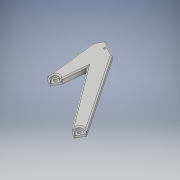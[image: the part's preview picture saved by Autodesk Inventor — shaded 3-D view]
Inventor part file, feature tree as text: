
AUTODESK INVENTOR PART (.ipt)
format: ipt  version: 2019.4 (Build 234330000, 330)  size: 259,584 bytes
history: native  units: mm
features: extrude x4, fillet x4, sketch x4
ambient origin geometry x8: Origin, YZ Plane, XZ Plane, XY Plane, X Axis, Y Axis, Z Axis, Center Point
bodies: Solid1 (feature_tree)
feature tree (12):
  extrude  "Extrusion1"  TaperAngle=90.0deg  [1 undecoded]
  extrude  "Extrusion2"  TaperAngle=150.0deg  [1 undecoded]
  extrude  "Extrusion4"  TaperAngle=150.0deg  [1 undecoded]
  fillet  "Fillet1"  Radius=231.766mm
  fillet  "Fillet2"  Radius=231.766mm
  fillet  "Fillet3"  Radius=5.25mm
  fillet  "Fillet4"  Radius=15.0mm
  extrude  "Extrusion5"  Depth=10.0mm
  sketch  "Sketch1"  dims[d0=100.0mm d1=90.0deg]
  sketch  "Sketch2"  dims[d2=100.0mm d3=150.0deg]
  sketch  "Sketch3"  dims[d4=100.0mm d5=150.0deg d6=231.766mm d7=231.766mm d8=5.25mm d10=15.0mm]
  sketch  "Sketch4"  dims[d11=120.0deg d12=10.0mm d13=100.0mm d14=70.0mm d15=25.307274mm d16=30.0mm d17=30.0deg d18=15.0mm d19=65.883mm d20=165.883mm d21=121.505mm d22=5.25mm d23=15.0mm d24=10.0mm d25=10.0mm d26=0.0mm d27=5.25mm d28=5.0mm d29=5.0mm d30=120.0deg d31=3.25mm d32=10.0mm d33=0.0mm d34=11.0mm d37=11.0mm d38=5.0mm d39=0.0mm d40=2.0mm d41=2.0mm d42=1.0mm d43=2.0mm d44=5.7mm d45=3.0mm d46=0.0mm]
note: 3 required parameter values undecoded (feature->parameter linkage not recoverable at this tier; creation-order binding heuristic only, values carry confidence <= 0.55)
